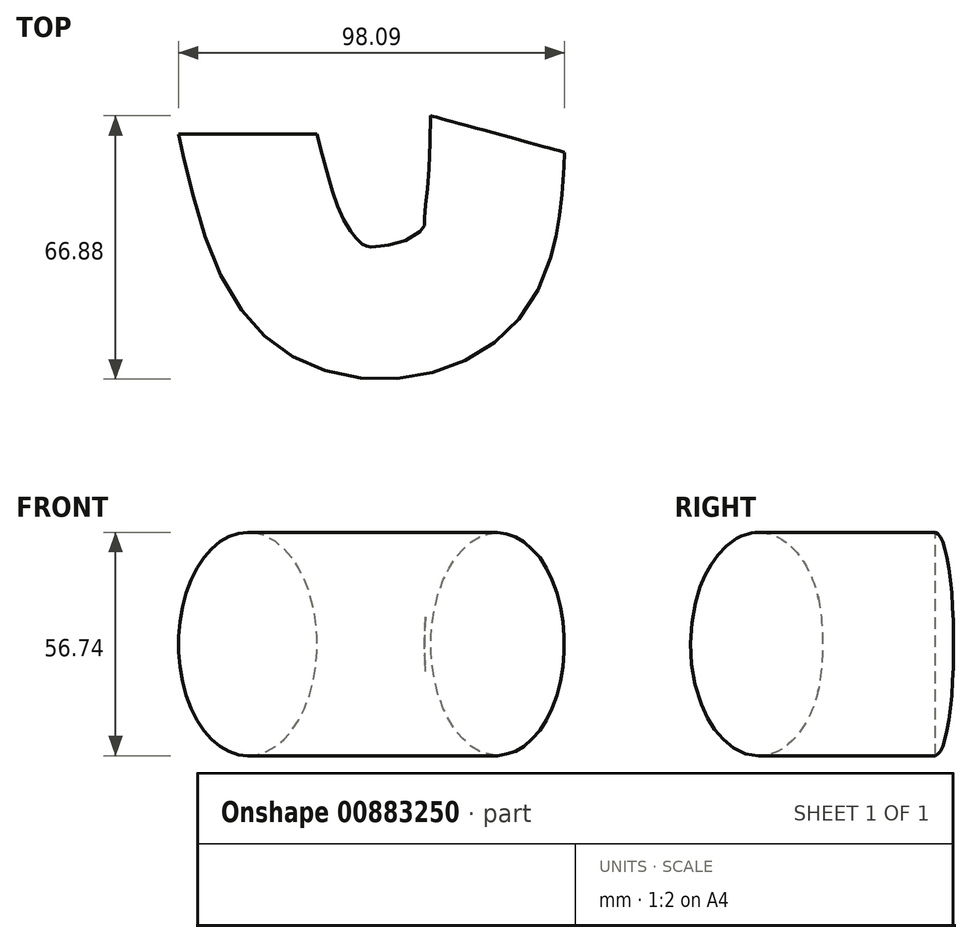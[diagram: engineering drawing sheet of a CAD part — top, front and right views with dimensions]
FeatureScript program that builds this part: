
annotation { "Feature Type Name" : "Feature", "Feature Type Description" : "" }
export const myFeature = defineFeature(function(context is Context, id is Id, definition is map)
    precondition{}
    {
        {
            var Q0;
            Q0=qCreatedBy(makeId("Front.planeOp"),FACE);
            var sketch = newSketch(context, id + "F0", { "sketchPlane" : qUnion([Q0])});
            skEllipse(sketch, "E0", {"center": v(0, 0) * mm, "majorRadius": 28.37 * mm, "minorRadius": 17.62 * mm, "majorAxis": v(0, -1)});
            skSolve(sketch);
        }
        {
            var Q0;
            Q0=qCreatedBy(makeId("Top.planeOp"),FACE);
            var sketch = newSketch(context, id + "F1", { "sketchPlane" : qUnion([Q0])});
            skFitSpline(sketch, "E1", {"points": [v(0, 0) * mm, v(19.63, -41.27) * mm, v(53.44, -38.11) * mm, v(63.47, 0) * mm], "startDerivative": vector(33.8, -143.67) * mm, "endDerivative": vector(4.88, 135.21) * mm});
            skSolve(sketch);
        }
        {
            var Q0;
            Q0 = qSketchRegion(id + "F0", true);
            var Q1;
            Q1=sQuery(id+"F1.wireOp",EDGE,"E1");
            sweep(context, id + "F2", {"profiles" : qUnion([Q0]), "path" : qUnion([Q1])});
        }
    });
